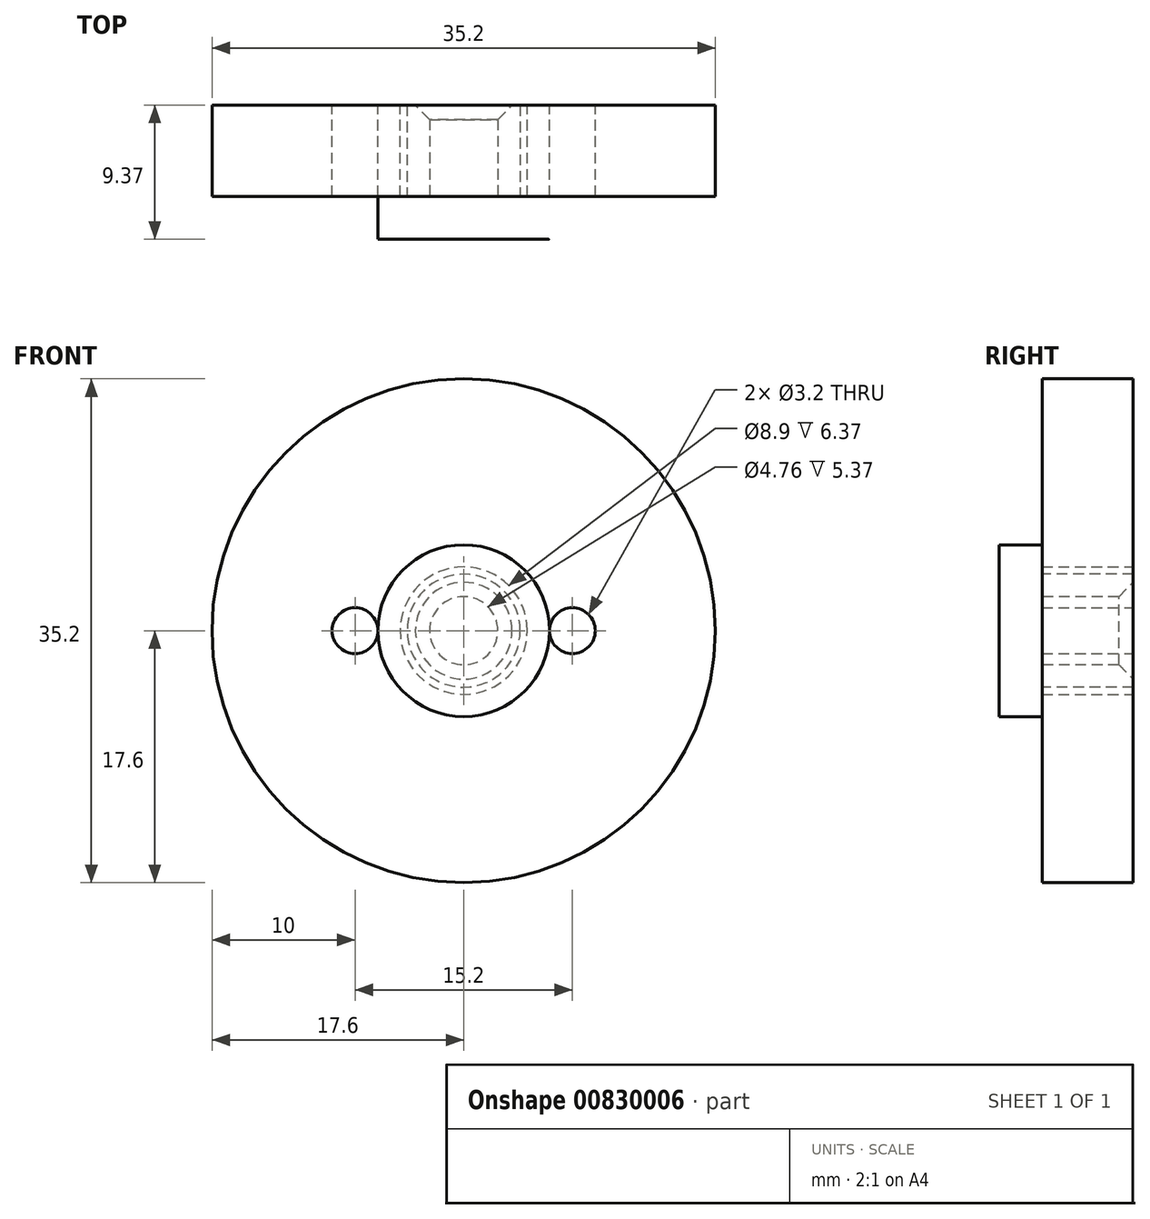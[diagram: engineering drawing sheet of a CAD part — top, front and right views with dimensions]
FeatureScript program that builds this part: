
annotation { "Feature Type Name" : "Feature", "Feature Type Description" : "" }
export const myFeature = defineFeature(function(context is Context, id is Id, definition is map)
    precondition{}
    {
        {
            var Q0;
            Q0=qCreatedBy(makeId("Front.planeOp"),FACE);
            var sketch = newSketch(context, id + "F0", { "sketchPlane" : qUnion([Q0])});
            skCircle(sketch, "E0", {"center": v(0, 0) * mm, "radius": 17.6 * mm});
            skCircle(sketch, "E1", {"center": v(0, 0) * mm, "radius": 4.45 * mm});
            skLineSegment(sketch, "E2", {"start": v(17.6, 0) * mm, "end": v(-17.6, 0) * mm, "construction": true});
            skCircle(sketch, "E3", {"center": v(-7.6, 0) * mm, "radius": 1.6 * mm});
            skCircle(sketch, "E4", {"center": v(7.6, 0) * mm, "radius": 1.6 * mm});
            skSolve(sketch);
        }
        {
            var Q0;
            Q0=makeQuery(id+"F0.imprint","IMPRINT",FACE,{"disambiguationData":[TD([[makeQuery(id+"F0.imprint","IMPRINT",EDGE,{"derivedFrom":sQuery(id+"F0.wireOp",EDGE,"E0")}),1.0]])]});
            extrude(context, id + "F1", {"entities" : qUnion([Q0]), "depth" : 6.37 * mm, "offsetDistance" : 25 * mm});
        }
        {
            var Q0;
            Q0=makeQuery(id+"F1.opExtrude","CAP_FACE",FACE,{"disambiguationData":[OSD([sQuery(id+"F0.wireOp",EDGE,"E0"),sQuery(id+"F0.wireOp",EDGE,"E1"),sQuery(id+"F0.wireOp",EDGE,"E3"),sQuery(id+"F0.wireOp",EDGE,"E4")])],"isStart":false});
            var sketch = newSketch(context, id + "F2", { "sketchPlane" : qUnion([Q0])});
            skCircle(sketch, "E5", {"center": v(0, 0) * mm, "radius": 2.38 * mm});
            skCircle(sketch, "E6.0", {"center": v(0, 0) * mm, "radius": 3.95 * mm});
            skCircle(sketch, "E7", {"center": v(0, 0) * mm, "radius": 6 * mm});
            skSolve(sketch);
        }
        {
            var Q0;
            Q0=makeQuery(id+"F2.imprint","IMPRINT",FACE,{"disambiguationData":[TD([[makeQuery(id+"F2.imprint","IMPRINT",EDGE,{"derivedFrom":sQuery(id+"F2.wireOp",EDGE,"E5")}),-1.0]])]});
            var Q1;
            Q1=makeQuery(id+"F1.opExtrude","CAP_FACE",FACE,{"disambiguationData":[OSD([sQuery(id+"F0.wireOp",EDGE,"E0"),sQuery(id+"F0.wireOp",EDGE,"E1"),sQuery(id+"F0.wireOp",EDGE,"E3"),sQuery(id+"F0.wireOp",EDGE,"E4")])],"isStart":true});
            extrude(context, id + "F3", {"entities" : qUnion([Q0]), "endBound" : BoundingType.UP_TO_SURFACE, "oppositeDirection" : true, "depth" : 25 * mm, "endBoundEntityFace" : qUnion([Q1]), "offsetDistance" : 25 * mm});
        }
        {
            var Q0;
            Q0=makeQuery(id+"F2.imprint","IMPRINT",FACE,{"disambiguationData":[TD([[makeQuery(id+"F2.imprint","IMPRINT",EDGE,{"derivedFrom":makeQuery(id+"F1.opExtrude","CAP_EDGE",EDGE,{"disambiguationData":[OSD([sQuery(id+"F0.wireOp",EDGE,"E1")])],"isStart":false})}),-1.0]])]});
            var Q1;
            Q1=makeQuery(id+"F2.imprint","IMPRINT",FACE,{"disambiguationData":[TD([[makeQuery(id+"F2.imprint","IMPRINT",EDGE,{"derivedFrom":sQuery(id+"F2.wireOp",EDGE,"E6.0")}),-1.0]])]});
            var Q2;
            Q2=makeQuery(id+"F2.imprint","IMPRINT",FACE,{"disambiguationData":[TD([[makeQuery(id+"F2.imprint","IMPRINT",EDGE,{"derivedFrom":sQuery(id+"F2.wireOp",EDGE,"E5")}),-1.0]])]});
            var Q3;
            Q3=makeQuery(id+"F2.imprint","IMPRINT",FACE,{"disambiguationData":[TD([[makeQuery(id+"F2.imprint","IMPRINT",EDGE,{"derivedFrom":sQuery(id+"F2.wireOp",EDGE,"E5")}),1.0]])]});
            extrude(context, id + "F4", {"entities" : qUnion([Q0, Q1, Q2, Q3]), "operationType" : NewBodyOperationType.ADD, "depth" : 3 * mm, "offsetDistance" : 25 * mm});
        }
        {
            var Q0;
            Q0=makeQuery(id+"F3.opExtrude","CAP_EDGE",EDGE,{"disambiguationData":[OSD([sQuery(id+"F2.wireOp",EDGE,"E5")])],"isStart":false});
            chamfer(context, id + "F5", {"entities" : qUnion([Q0]), "width" : 1 * mm, "tangentPropagation" : true});
        }
    });
